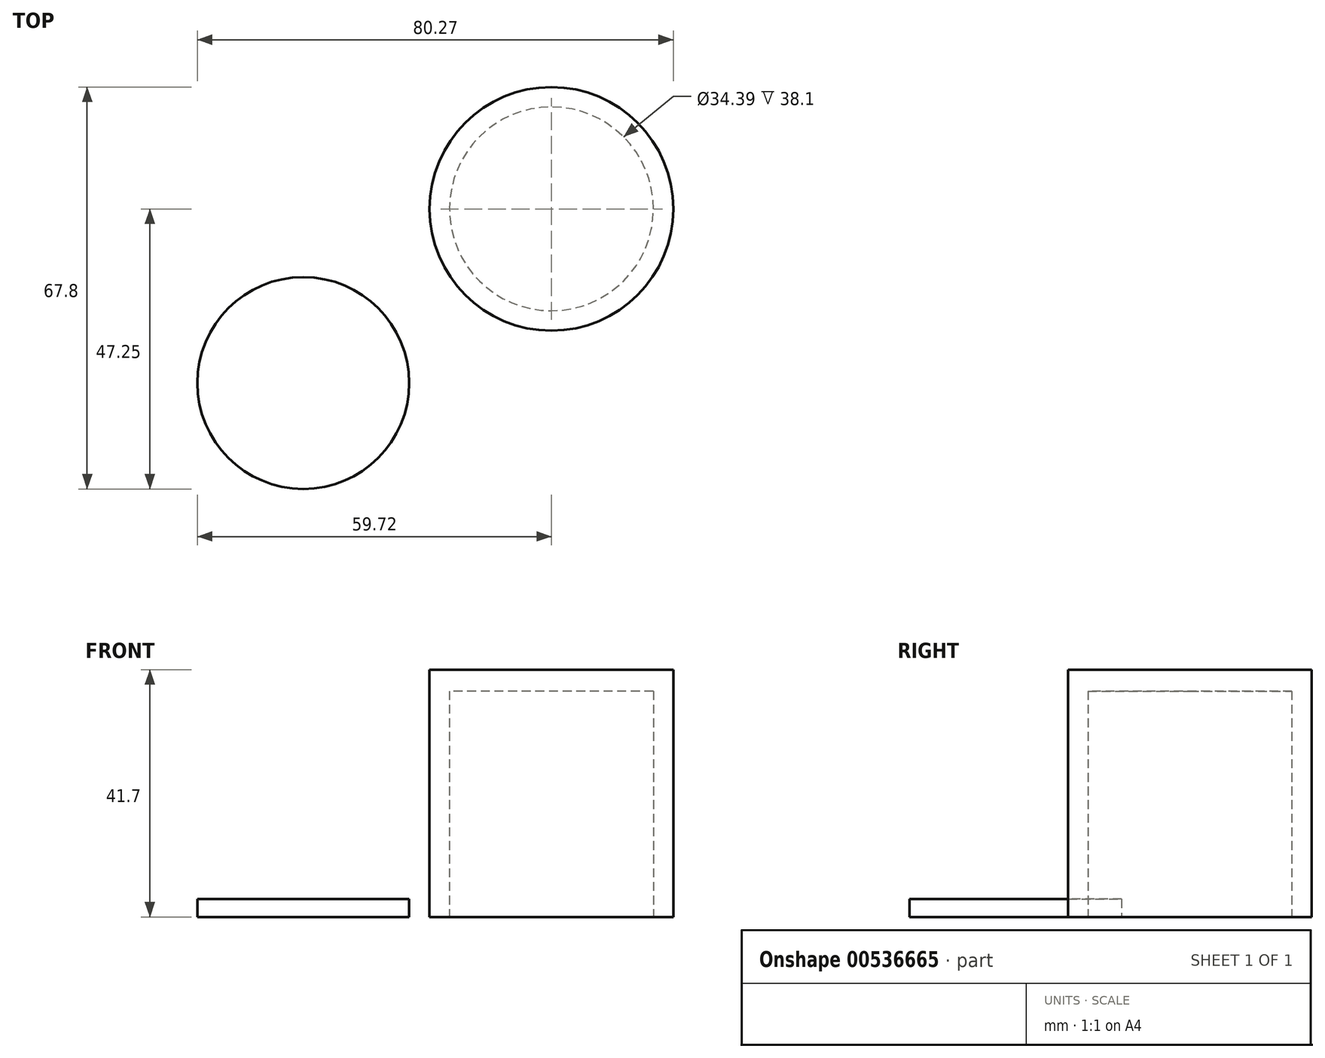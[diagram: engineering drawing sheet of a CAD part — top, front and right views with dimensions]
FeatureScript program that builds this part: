
annotation { "Feature Type Name" : "Feature", "Feature Type Description" : "" }
export const myFeature = defineFeature(function(context is Context, id is Id, definition is map)
    precondition{}
    {
        {
            var Q0;
            Q0=qCreatedBy(makeId("Top.planeOp"),FACE);
            var sketch = newSketch(context, id + "F0", { "sketchPlane" : qUnion([Q0])});
            skCircle(sketch, "E0", {"center": v(0, 0) * mm, "radius": 20.55 * mm});
            skSolve(sketch);
        }
        {
            var Q0;
            Q0=makeQuery(id+"F0.imprint","IMPRINT",FACE,{"disambiguationData":[TD([[makeQuery(id+"F0.imprint","IMPRINT",EDGE,{"derivedFrom":sQuery(id+"F0.wireOp",EDGE,"E0")}),1.0]])]});
            extrude(context, id + "F1", {"entities" : qUnion([Q0]), "depth" : 41.7 * mm, "offsetDistance" : 25.4 * mm});
        }
        {
            var Q0;
            Q0=qCreatedBy(makeId("Top.planeOp"),FACE);
            var sketch = newSketch(context, id + "F2", { "sketchPlane" : qUnion([Q0])});
            skCircle(sketch, "E1", {"center": v(0, 0) * mm, "radius": 17.2 * mm});
            skSolve(sketch);
        }
        {
            var Q0;
            Q0 = qSketchRegion(id + "F2", true);
            extrude(context, id + "F3", {"entities" : qUnion([Q0]), "operationType" : NewBodyOperationType.REMOVE, "depth" : 38.1 * mm, "offsetDistance" : 25.4 * mm});
        }
        {
            var Q0;
            Q0=qCreatedBy(makeId("Top.planeOp"),FACE);
            var sketch = newSketch(context, id + "F4", { "sketchPlane" : qUnion([Q0])});
            skCircle(sketch, "E2", {"center": v(-41.85, -29.38) * mm, "radius": 17.87 * mm});
            skSolve(sketch);
        }
        {
            var Q0;
            Q0=makeQuery(id+"F4.imprint","IMPRINT",FACE,{"disambiguationData":[TD([[makeQuery(id+"F4.imprint","IMPRINT",EDGE,{"derivedFrom":sQuery(id+"F4.wireOp",EDGE,"E2")}),1.0]])]});
            extrude(context, id + "F5", {"entities" : qUnion([Q0]), "depth" : 3 * mm, "offsetDistance" : 25.4 * mm});
        }
    });
